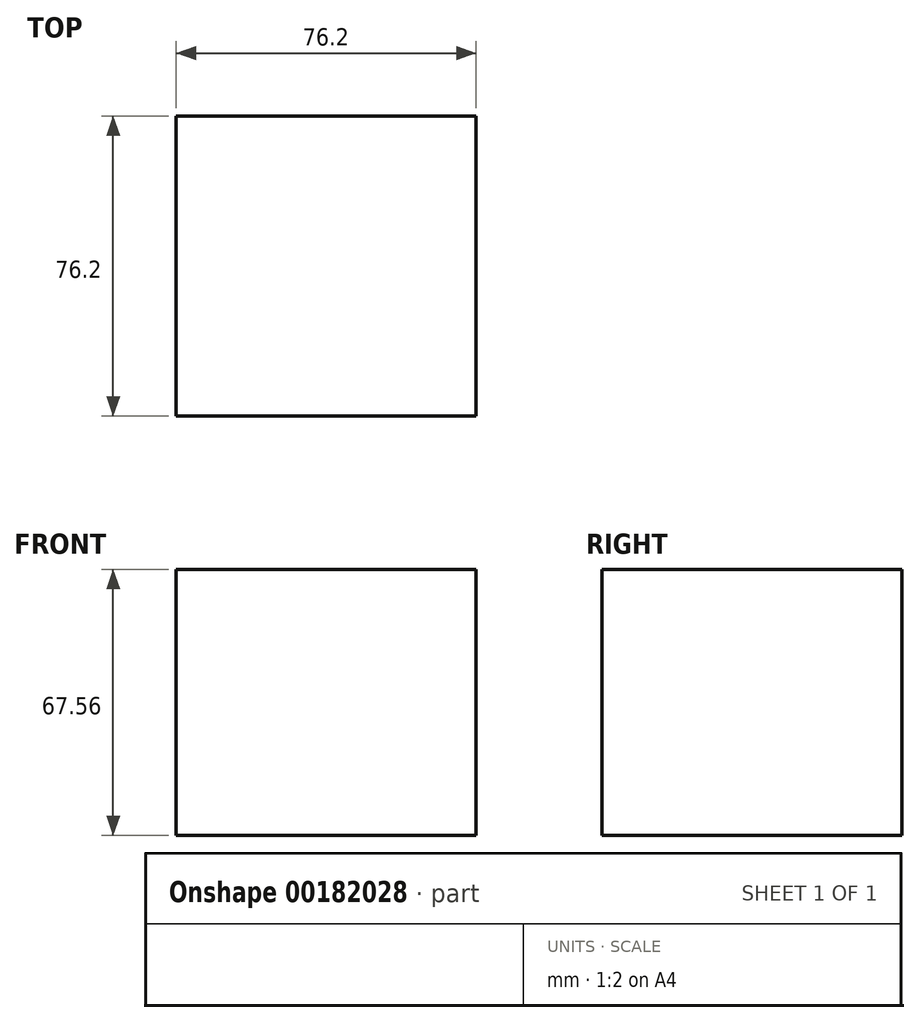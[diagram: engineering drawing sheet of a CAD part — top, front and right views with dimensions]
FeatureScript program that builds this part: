
annotation { "Feature Type Name" : "Feature", "Feature Type Description" : "" }
export const myFeature = defineFeature(function(context is Context, id is Id, definition is map)
    precondition{}
    {
        {
            var Q0;
            Q0=qCreatedBy(makeId("Top.planeOp"),FACE);
            var sketch = newSketch(context, id + "F0", { "sketchPlane" : qUnion([Q0])});
            skLineSegment(sketch, "E0.bottom", {"start": v(38.1, -38.1) * mm, "end": v(-38.1, -38.1) * mm});
            skLineSegment(sketch, "E0.top", {"start": v(38.1, 38.1) * mm, "end": v(-38.1, 38.1) * mm});
            skLineSegment(sketch, "E0.left", {"start": v(38.1, -38.1) * mm, "end": v(38.1, 38.1) * mm});
            skLineSegment(sketch, "E0.right", {"start": v(-38.1, -38.1) * mm, "end": v(-38.1, 38.1) * mm});
            skPoint(sketch, "E0.middle", {"position": v(0, 0) * mm});
            skSolve(sketch);
        }
        {
            var Q0;
            Q0=makeQuery(id+"F0.imprint","IMPRINT",FACE,{"disambiguationData":[TD([[makeQuery(id+"F0.imprint","IMPRINT",EDGE,{"derivedFrom":sQuery(id+"F0.wireOp",EDGE,"E0.bottom")}),-1.0]])]});
            extrude(context, id + "F1", {"entities" : qUnion([Q0]), "depth" : 67.56 * mm});
        }
    });
